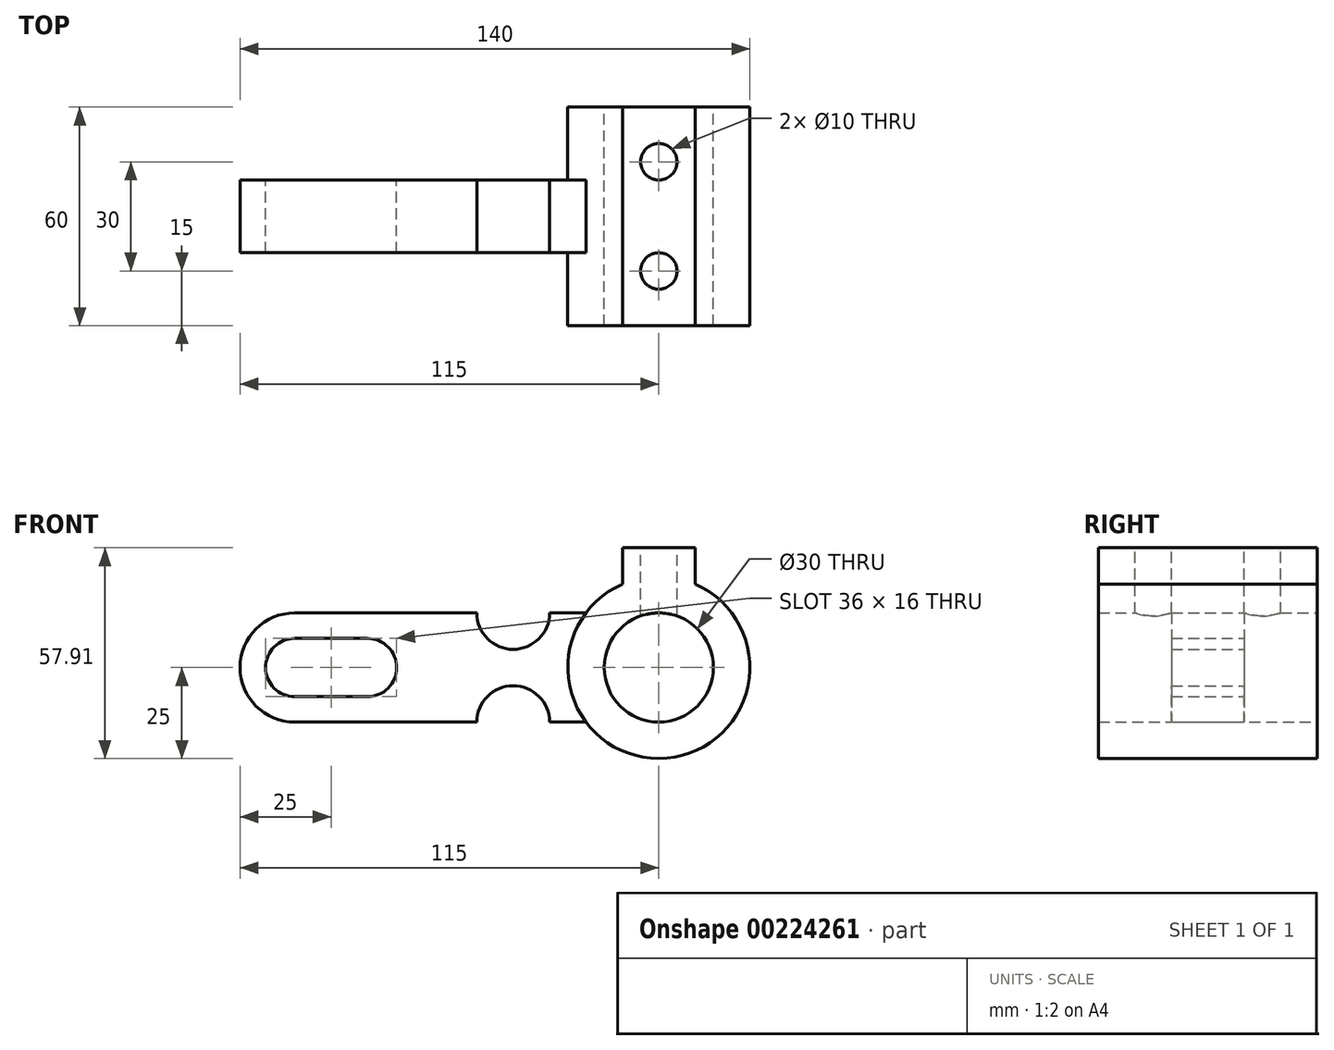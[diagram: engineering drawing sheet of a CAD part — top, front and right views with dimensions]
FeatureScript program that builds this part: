
annotation { "Feature Type Name" : "Feature", "Feature Type Description" : "" }
export const myFeature = defineFeature(function(context is Context, id is Id, definition is map)
    precondition{}
    {
        {
            var Q0;
            Q0=qCreatedBy(makeId("Front.planeOp"),FACE);
            var sketch = newSketch(context, id + "F0", { "sketchPlane" : qUnion([Q0])});
            skArc(sketch, "E0", {"start": v(0, 8) * mm, "mid": v(-8, 0) * mm, "end": v(0, -8) * mm});
            skArc(sketch, "E1", {"start": v(0, 15) * mm, "mid": v(-15, 0) * mm, "end": v(0, -15) * mm});
            skLineSegment(sketch, "E2", {"start": v(-15, 0) * mm, "end": v(125, 0) * mm, "construction": true});
            skLineSegment(sketch, "E3", {"start": v(0, 15) * mm, "end": v(50, 15) * mm});
            skLineSegment(sketch, "E4", {"start": v(0, -15) * mm, "end": v(50, -15) * mm});
            skArc(sketch, "E5", {"start": v(20, -8) * mm, "mid": v(28, 0) * mm, "end": v(20, 8) * mm});
            skLineSegment(sketch, "E6", {"start": v(0, 8) * mm, "end": v(20, 8) * mm});
            skLineSegment(sketch, "E7", {"start": v(0, -8) * mm, "end": v(20, -8) * mm});
            skArc(sketch, "E8", {"start": v(70, -15) * mm, "mid": v(60, -5) * mm, "end": v(50, -15) * mm});
            skArc(sketch, "E9", {"start": v(50, 15) * mm, "mid": v(60, 5) * mm, "end": v(70, 15) * mm});
            skLineSegment(sketch, "E10", {"start": v(70, 15) * mm, "end": v(80, 15) * mm});
            skLineSegment(sketch, "E11", {"start": v(74.9, -15) * mm, "end": v(80, -15) * mm});
            skArc(sketch, "E12", {"start": v(90, 22.91) * mm, "mid": v(100, -25) * mm, "end": v(110, 22.91) * mm});
            skCircle(sketch, "E13", {"center": v(100, 0) * mm, "radius": 15 * mm});
            skPoint(sketch, "E14.orphan", {"position": v(89.29, 15) * mm});
            skPoint(sketch, "E15.orphan", {"position": v(89.29, -15) * mm});
            skLineSegment(sketch, "E16.trimOffspring", {"start": v(70, -15) * mm, "end": v(74.9, -15) * mm});
            skPoint(sketch, "E17.orphan", {"position": v(75, 0) * mm});
            skLineSegment(sketch, "E18", {"start": v(100, 36.99) * mm, "end": v(100, -44.2) * mm, "construction": true});
            skLineSegment(sketch, "E19.bottom", {"start": v(110, 32.91) * mm, "end": v(90, 32.91) * mm});
            skLineSegment(sketch, "E19.left", {"start": v(110, 32.91) * mm, "end": v(110, 22.91) * mm});
            skLineSegment(sketch, "E19.right", {"start": v(90, 32.91) * mm, "end": v(90, 22.91) * mm});
            skPoint(sketch, "E19.middle", {"position": v(100, 27.91) * mm});
            skLineSegment(sketch, "E20", {"start": v(110, 22.91) * mm, "end": v(110, 22.91) * mm});
            skLineSegment(sketch, "E21", {"start": v(90, 22.91) * mm, "end": v(90, 22.91) * mm});
            skSolve(sketch);
        }
        {
            var Q0;
            Q0=makeQuery(id+"F0.imprint","IMPRINT",FACE,{"disambiguationData":[TD([[makeQuery(id+"F0.imprint","IMPRINT",EDGE,{"derivedFrom":sQuery(id+"F0.wireOp",EDGE,"E13")}),-1.0]])]});
            extrude(context, id + "F1", {"entities" : qUnion([Q0]), "endBound" : BoundingType.SYMMETRIC, "depth" : 60 * mm});
        }
        {
            var Q0;
            Q0=makeQuery(id+"F0.imprint","IMPRINT",FACE,{"disambiguationData":[TD([[makeQuery(id+"F0.imprint","IMPRINT",EDGE,{"derivedFrom":sQuery(id+"F0.wireOp",EDGE,"E0")}),-1.0]])]});
            extrude(context, id + "F2", {"entities" : qUnion([Q0]), "operationType" : NewBodyOperationType.ADD, "endBound" : BoundingType.SYMMETRIC, "depth" : 20 * mm});
        }
        {
            var Q0;
            Q0=makeQuery(id+"F1.opExtrude","SWEPT_FACE",FACE,{"disambiguationData":[OSD([sQuery(id+"F0.wireOp",EDGE,"E19.bottom")])]});
            var sketch = newSketch(context, id + "F3", { "sketchPlane" : qUnion([Q0])});
            skCircle(sketch, "E22", {"center": v(100, 15) * mm, "radius": 5 * mm});
            skCircle(sketch, "E23", {"center": v(100, -15) * mm, "radius": 5 * mm});
            skSolve(sketch);
        }
        {
            var Q0;
            Q0 = qSketchRegion(id + "F3", true);
            extrude(context, id + "F4", {"entities" : qUnion([Q0]), "operationType" : NewBodyOperationType.REMOVE, "oppositeDirection" : true, "depth" : 20 * mm});
        }
    });
